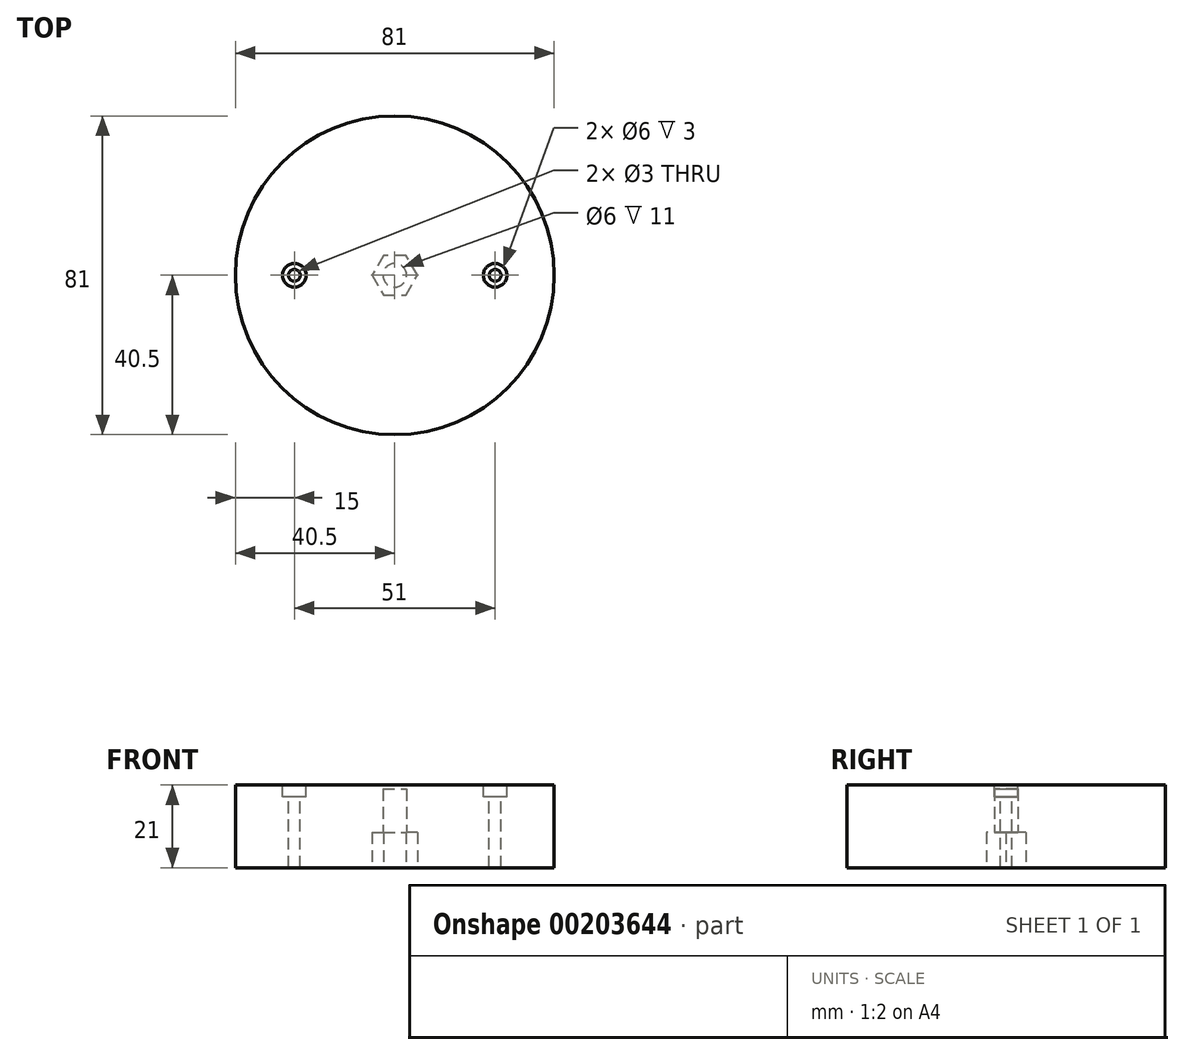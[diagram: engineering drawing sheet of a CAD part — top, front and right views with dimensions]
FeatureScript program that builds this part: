
annotation { "Feature Type Name" : "Feature", "Feature Type Description" : "" }
export const myFeature = defineFeature(function(context is Context, id is Id, definition is map)
    precondition{}
    {
        {
            var Q0;
            Q0=qCreatedBy(makeId("Top.planeOp"),FACE);
            var sketch = newSketch(context, id + "F0", { "sketchPlane" : qUnion([Q0])});
            skCircle(sketch, "E0", {"center": v(0, 0) * mm, "radius": 40.5 * mm});
            skSolve(sketch);
        }
        {
            var Q0;
            Q0=makeQuery(id+"F0.imprint","IMPRINT",FACE,{"disambiguationData":[TD([[makeQuery(id+"F0.imprint","IMPRINT",EDGE,{"derivedFrom":sQuery(id+"F0.wireOp",EDGE,"E0")}),1.0]])]});
            extrude(context, id + "F1", {"entities" : qUnion([Q0]), "depth" : 21 * mm});
        }
        {
            var Q0;
            Q0=makeQuery(id+"F1.opExtrude","CAP_FACE",FACE,{"disambiguationData":[OSD([sQuery(id+"F0.wireOp",EDGE,"E0")])],"isStart":false});
            var sketch = newSketch(context, id + "F2", { "sketchPlane" : qUnion([Q0])});
            skCircle(sketch, "E1", {"center": v(25.5, 0) * mm, "radius": 3 * mm});
            skCircle(sketch, "E2", {"center": v(-25.5, 0) * mm, "radius": 3 * mm});
            skSolve(sketch);
        }
        {
            var Q0;
            Q0=makeQuery(id+"F2.imprint","IMPRINT",FACE,{"disambiguationData":[TD([[makeQuery(id+"F2.imprint","IMPRINT",EDGE,{"derivedFrom":sQuery(id+"F2.wireOp",EDGE,"E2")}),1.0]])]});
            var Q1;
            Q1=makeQuery(id+"F2.imprint","IMPRINT",FACE,{"disambiguationData":[TD([[makeQuery(id+"F2.imprint","IMPRINT",EDGE,{"derivedFrom":sQuery(id+"F2.wireOp",EDGE,"E1")}),1.0]])]});
            extrude(context, id + "F3", {"entities" : qUnion([Q0, Q1]), "operationType" : NewBodyOperationType.REMOVE, "oppositeDirection" : true, "depth" : 3 * mm});
        }
        {
            var Q0;
            Q0=makeQuery(id+"F3.boolean.opBoolean","COPY",FACE,{"derivedFrom":makeQuery(id+"F3.opExtrude","CAP_FACE",FACE,{"disambiguationData":[OSD([sQuery(id+"F2.wireOp",EDGE,"E2")])],"isStart":false})});
            var sketch = newSketch(context, id + "F4", { "sketchPlane" : qUnion([Q0])});
            skCircle(sketch, "E3", {"center": v(-25.5, 0) * mm, "radius": 1.5 * mm});
            skCircle(sketch, "E4.MirrorC", {"center": v(25.5, 0) * mm, "radius": 1.5 * mm});
            skSolve(sketch);
        }
        {
            var Q0;
            Q0 = qSketchRegion(id + "F4", true);
            extrude(context, id + "F5", {"entities" : qUnion([Q0]), "operationType" : NewBodyOperationType.REMOVE, "oppositeDirection" : true, "depth" : 25 * mm});
        }
        {
            var Q0;
            Q0=makeQuery(id+"F1.opExtrude","CAP_FACE",FACE,{"disambiguationData":[OSD([sQuery(id+"F0.wireOp",EDGE,"E0")])],"isStart":true});
            var sketch = newSketch(context, id + "F6", { "sketchPlane" : qUnion([Q0])});
            skCircle(sketch, "E5.cCircle", {"center": v(0, 0) * mm, "radius": 5 * mm, "construction": true});
            skLineSegment(sketch, "E5.0", {"start": v(-2.89, 5) * mm, "end": v(2.89, 5) * mm});
            skLineSegment(sketch, "E5.1", {"start": v(2.89, 5) * mm, "end": v(5.77, 0) * mm});
            skLineSegment(sketch, "E5.2", {"start": v(5.77, 0) * mm, "end": v(2.89, -5) * mm});
            skLineSegment(sketch, "E5.3", {"start": v(2.89, -5) * mm, "end": v(-2.89, -5) * mm});
            skLineSegment(sketch, "E5.4", {"start": v(-2.89, -5) * mm, "end": v(-5.77, 0) * mm});
            skLineSegment(sketch, "E5.5", {"start": v(-5.77, 0) * mm, "end": v(-2.89, 5) * mm});
            skPoint(sketch, "E5.0.midPoint", {"position": v(0, 5) * mm});
            skSolve(sketch);
        }
        {
            var Q0;
            Q0=makeQuery(id+"F6.imprint","IMPRINT",FACE,{"disambiguationData":[TD([[makeQuery(id+"F6.imprint","IMPRINT",EDGE,{"derivedFrom":sQuery(id+"F6.wireOp",EDGE,"E5.0")}),-1.0]])]});
            extrude(context, id + "F7", {"entities" : qUnion([Q0]), "operationType" : NewBodyOperationType.REMOVE, "oppositeDirection" : true, "depth" : 9 * mm});
        }
        {
            var Q0;
            Q0=makeQuery(id+"F1.opExtrude","CAP_FACE",FACE,{"disambiguationData":[OSD([sQuery(id+"F0.wireOp",EDGE,"E0")])],"isStart":true});
            var sketch = newSketch(context, id + "F8", { "sketchPlane" : qUnion([Q0])});
            skCircle(sketch, "E6", {"center": v(0, 0) * mm, "radius": 3 * mm});
            skSolve(sketch);
        }
        {
            var Q0;
            Q0=makeQuery(id+"F8.imprint","IMPRINT",FACE,{"disambiguationData":[TD([[makeQuery(id+"F8.imprint","IMPRINT",EDGE,{"derivedFrom":sQuery(id+"F8.wireOp",EDGE,"E6")}),1.0]])]});
            extrude(context, id + "F9", {"entities" : qUnion([Q0]), "operationType" : NewBodyOperationType.REMOVE, "oppositeDirection" : true, "depth" : 20 * mm});
        }
        {
            var Q0;
            Q0=qCreatedBy(makeId("Front.planeOp"),FACE);
            cPlane(context, id + "F10", {"entities" : qUnion([Q0]), "cplaneType" : CPlaneType.OFFSET, "offset" : 3 * mm, "width" : 150 * mm, "height" : 150 * mm});
        }
    });
